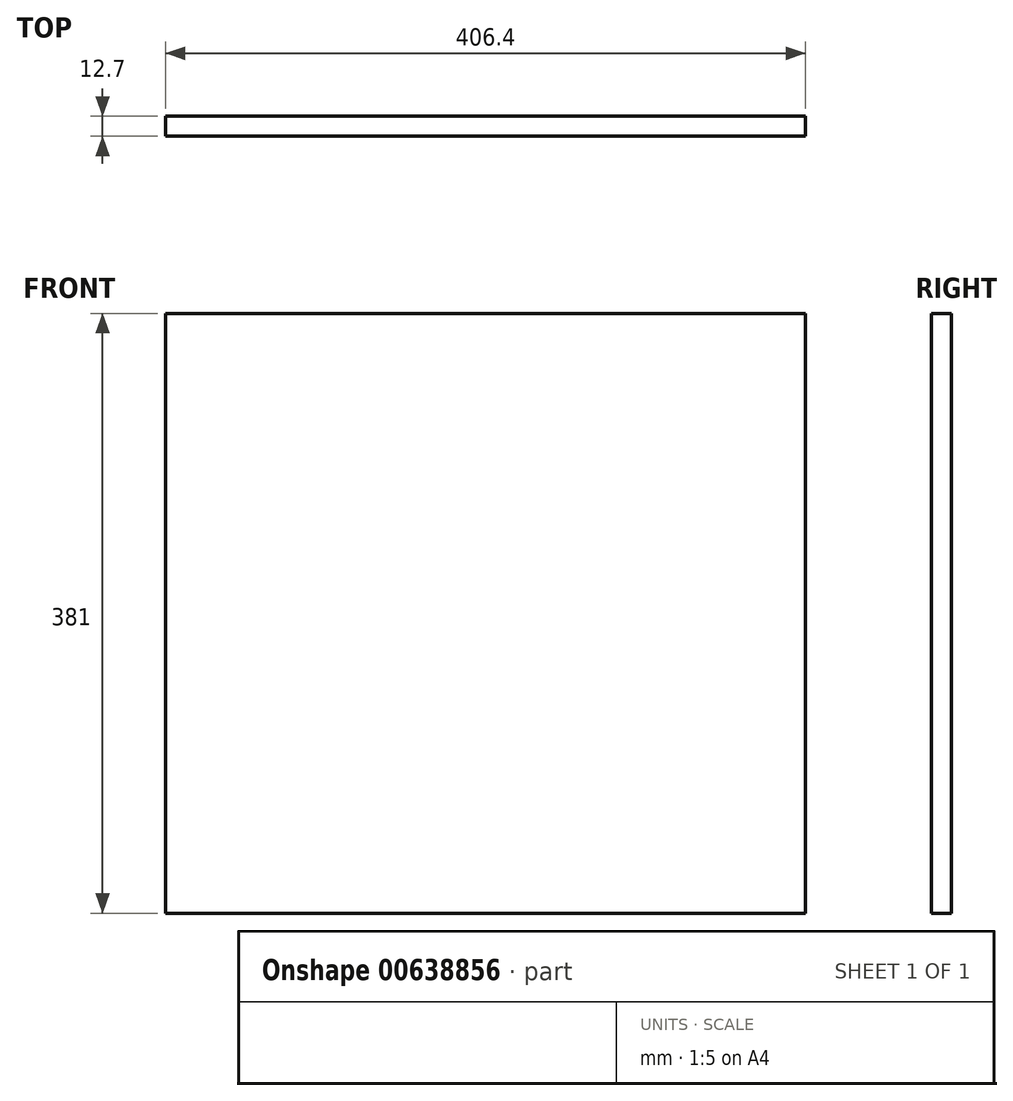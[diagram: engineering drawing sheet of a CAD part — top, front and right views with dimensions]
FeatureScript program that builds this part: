
annotation { "Feature Type Name" : "Feature", "Feature Type Description" : "" }
export const myFeature = defineFeature(function(context is Context, id is Id, definition is map)
    precondition{}
    {
        {
            var Q0;
            Q0=qCreatedBy(makeId("Front.planeOp"),FACE);
            var sketch = newSketch(context, id + "F0", { "sketchPlane" : qUnion([Q0])});
            skLineSegment(sketch, "E0.bottom", {"start": v(203.2, 190.5) * mm, "end": v(-203.2, 190.5) * mm});
            skLineSegment(sketch, "E0.top", {"start": v(203.2, -190.5) * mm, "end": v(-203.2, -190.5) * mm});
            skLineSegment(sketch, "E0.left", {"start": v(203.2, 190.5) * mm, "end": v(203.2, -190.5) * mm});
            skLineSegment(sketch, "E0.right", {"start": v(-203.2, 190.5) * mm, "end": v(-203.2, -190.5) * mm});
            skPoint(sketch, "E0.middle", {"position": v(0, 0) * mm});
            skSolve(sketch);
        }
        {
            var Q0;
            Q0=makeQuery(id+"F0.imprint","IMPRINT",FACE,{"disambiguationData":[TD([[makeQuery(id+"F0.imprint","IMPRINT",EDGE,{"derivedFrom":sQuery(id+"F0.wireOp",EDGE,"E0.bottom")}),1.0]])]});
            extrude(context, id + "F1", {"entities" : qUnion([Q0]), "depth" : 12.7 * mm, "offsetDistance" : 25.4 * mm});
        }
    });
